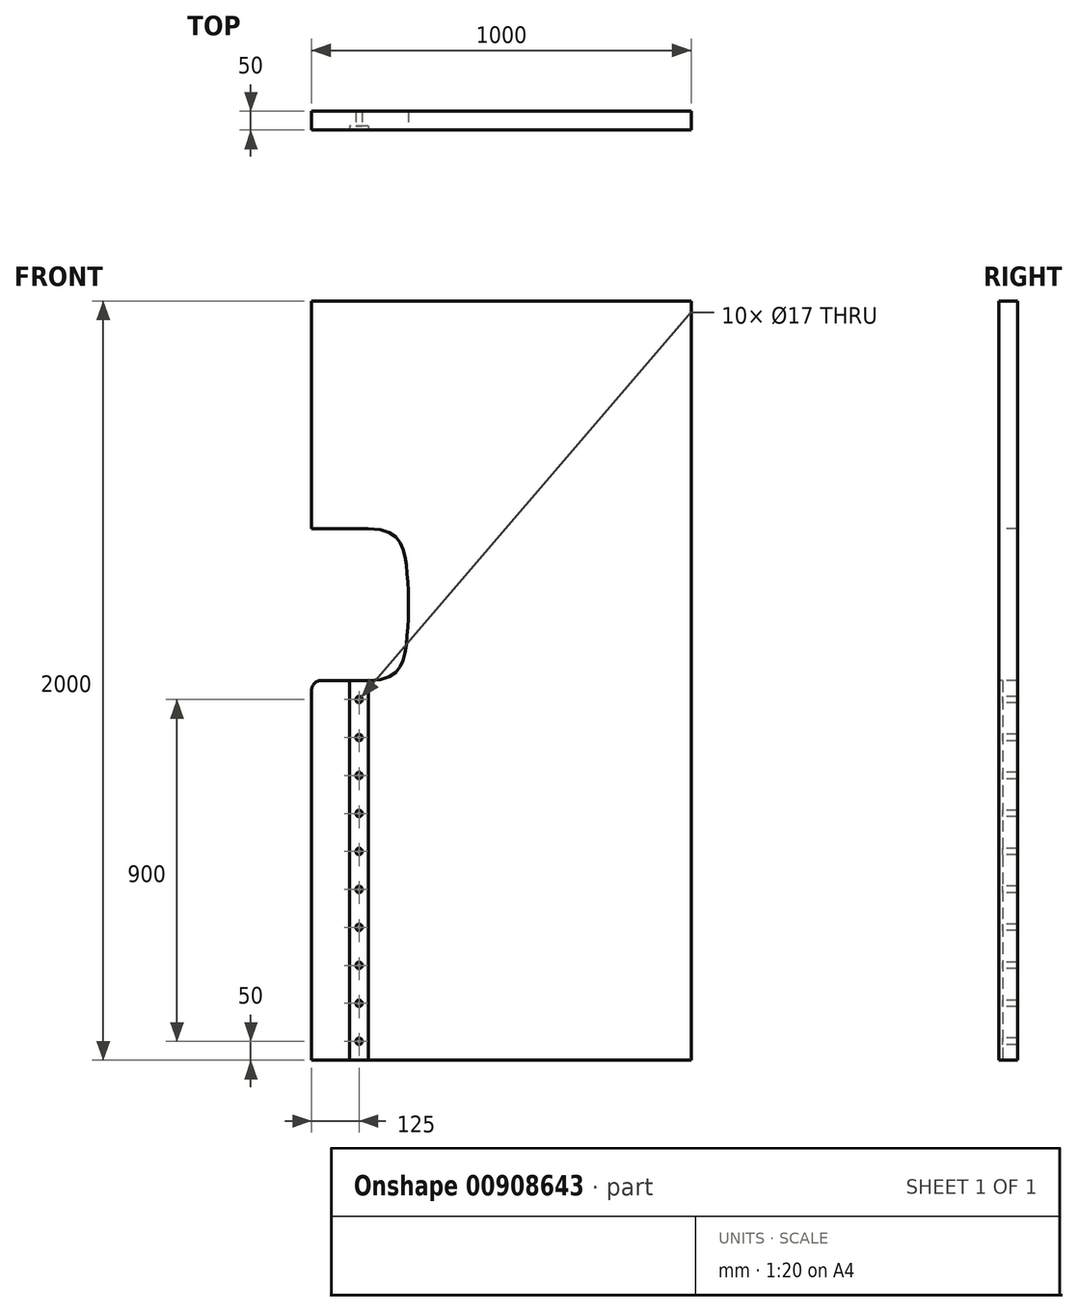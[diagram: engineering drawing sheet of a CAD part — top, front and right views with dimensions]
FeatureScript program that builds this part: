
annotation { "Feature Type Name" : "Feature", "Feature Type Description" : "" }
export const myFeature = defineFeature(function(context is Context, id is Id, definition is map)
    precondition{}
    {
        {
            var Q0;
            Q0=qCreatedBy(makeId("Front.planeOp"),FACE);
            var sketch = newSketch(context, id + "F0", { "sketchPlane" : qUnion([Q0])});
            skLineSegment(sketch, "E0.bottom", {"start": v(500, 1000) * mm, "end": v(-500, 1000) * mm});
            skLineSegment(sketch, "E0.top", {"start": v(500, -1000) * mm, "end": v(-500, -1000) * mm});
            skLineSegment(sketch, "E0.left", {"start": v(500, 1000) * mm, "end": v(500, -1000) * mm});
            skLineSegment(sketch, "E0.right", {"start": v(-500, 1000) * mm, "end": v(-500, -1000) * mm});
            skPoint(sketch, "E0.middle", {"position": v(0, 0) * mm});
            skSolve(sketch);
        }
        {
            var Q0;
            Q0=makeQuery(id+"F0.imprint","IMPRINT",FACE,{"disambiguationData":[TD([[makeQuery(id+"F0.imprint","IMPRINT",EDGE,{"derivedFrom":sQuery(id+"F0.wireOp",EDGE,"E0.bottom")}),1.0]])]});
            extrude(context, id + "F1", {"entities" : qUnion([Q0]), "depth" : 50 * mm, "offsetDistance" : 25 * mm});
        }
        {
            var Q0;
            Q0=makeQuery(id+"F1.opExtrude","CAP_FACE",FACE,{"disambiguationData":[OSD([sQuery(id+"F0.wireOp",EDGE,"E0.bottom"),sQuery(id+"F0.wireOp",EDGE,"E0.top"),sQuery(id+"F0.wireOp",EDGE,"E0.left"),sQuery(id+"F0.wireOp",EDGE,"E0.right")])],"isStart":false});
            var sketch = newSketch(context, id + "F2", { "sketchPlane" : qUnion([Q0])});
            skLineSegment(sketch, "E1.bottom", {"start": v(-400, 0) * mm, "end": v(-350, 0) * mm});
            skLineSegment(sketch, "E1.top", {"start": v(-400, -1000) * mm, "end": v(-350, -1000) * mm});
            skLineSegment(sketch, "E1.left", {"start": v(-400, 0) * mm, "end": v(-400, -1000) * mm});
            skLineSegment(sketch, "E1.right", {"start": v(-350, 0) * mm, "end": v(-350, -1000) * mm});
            skPoint(sketch, "E2.visualSharp", {"position": v(-400, 0) * mm});
            skPoint(sketch, "E3.visualSharp", {"position": v(-350, 0) * mm});
            skSolve(sketch);
        }
        {
            var Q0;
            Q0=makeQuery(id+"F2.imprint","IMPRINT",FACE,{"disambiguationData":[TD([[makeQuery(id+"F2.imprint","IMPRINT",EDGE,{"derivedFrom":sQuery(id+"F2.wireOp",EDGE,"E1.bottom")}),-1.0]])]});
            extrude(context, id + "F3", {"entities" : qUnion([Q0]), "operationType" : NewBodyOperationType.REMOVE, "oppositeDirection" : true, "depth" : 10 * mm, "offsetDistance" : 25 * mm});
        }
        {
            var Q0;
            Q0=makeQuery(id+"F1.opExtrude","CAP_FACE",FACE,{"disambiguationData":[OSD([sQuery(id+"F0.wireOp",EDGE,"E0.bottom"),sQuery(id+"F0.wireOp",EDGE,"E0.top"),sQuery(id+"F0.wireOp",EDGE,"E0.left"),sQuery(id+"F0.wireOp",EDGE,"E0.right")])],"isStart":false});
            var sketch = newSketch(context, id + "F4", { "sketchPlane" : qUnion([Q0])});
            skLineSegment(sketch, "E4", {"start": v(-500, 0) * mm, "end": v(-350, 0) * mm});
            skLineSegment(sketch, "E5", {"start": v(-350, 400) * mm, "end": v(-500, 400) * mm});
            skLineSegment(sketch, "E6", {"start": v(-500, 400) * mm, "end": v(-500, 0) * mm});
            skPoint(sketch, "E7.visualSharp", {"position": v(-250, 0) * mm});
            skPoint(sketch, "E8.visualSharp", {"position": v(-250, 400) * mm});
            skFitSpline(sketch, "E9", {"points": [v(-350, 400) * mm, v(-250, 300) * mm, v(-250, 100) * mm, v(-350, 0) * mm], "startDerivative": vector(804.85, -3.53) * mm, "endDerivative": vector(-804.85, 0) * mm});
            skSolve(sketch);
        }
        {
            var Q0;
            Q0=makeQuery(id+"F4.imprint","IMPRINT",FACE,{"disambiguationData":[TD([[makeQuery(id+"F4.imprint","IMPRINT",EDGE,{"derivedFrom":sQuery(id+"F4.wireOp",EDGE,"E5")}),1.0]])]});
            extrude(context, id + "F5", {"entities" : qUnion([Q0]), "operationType" : NewBodyOperationType.REMOVE, "endBound" : BoundingType.THROUGH_ALL, "oppositeDirection" : true, "depth" : 25 * mm, "offsetDistance" : 25 * mm});
        }
        {
            var Q0;
            Q0=makeQuery(id+"F5.boolean.opBoolean","COPY",EDGE,{"derivedFrom":makeQuery(id+"F5.opExtrude","SWEPT_EDGE",EDGE,{"disambiguationData":[OSD([sQuery(id+"F0.wireOp",EDGE,"E0.right"),sQuery(id+"F4.wireOp",EDGE,"E5"),sQuery(id+"F4.wireOp",EDGE,"E6")])]})});
            var Q1;
            Q1=makeQuery(id+"F5.boolean.opBoolean","COPY",EDGE,{"derivedFrom":makeQuery(id+"F5.opExtrude","SWEPT_EDGE",EDGE,{"disambiguationData":[OSD([sQuery(id+"F0.wireOp",EDGE,"E0.right"),sQuery(id+"F4.wireOp",EDGE,"E4"),sQuery(id+"F4.wireOp",EDGE,"E6")])]})});
            fillet(context, id + "F6", {"entities" : qUnion([Q0, Q1]), "radius" : 25 * mm, "tangentPropagation" : true, "allowEdgeOverflow" : false});
        }
        {
            var Q0;
            Q0=makeQuery(id+"F3.boolean.opBoolean","COPY",FACE,{"derivedFrom":makeQuery(id+"F3.opExtrude","CAP_FACE",FACE,{"disambiguationData":[OSD([sQuery(id+"F2.wireOp",EDGE,"E1.bottom"),sQuery(id+"F2.wireOp",EDGE,"E1.top"),sQuery(id+"F2.wireOp",EDGE,"E1.left"),sQuery(id+"F2.wireOp",EDGE,"E1.right")])],"isStart":false})});
            var sketch = newSketch(context, id + "F7", { "sketchPlane" : qUnion([Q0])});
            skCircle(sketch, "E10", {"center": v(-375, -950) * mm, "radius": 8.5 * mm});
            skCircle(sketch, "E11.0.1.0", {"center": v(-375, -850) * mm, "radius": 8.5 * mm});
            skCircle(sketch, "E11.0.2.0", {"center": v(-375, -750) * mm, "radius": 8.5 * mm});
            skCircle(sketch, "E11.0.3.0", {"center": v(-375, -650) * mm, "radius": 8.5 * mm});
            skCircle(sketch, "E11.0.4.0", {"center": v(-375, -550) * mm, "radius": 8.5 * mm});
            skCircle(sketch, "E11.0.5.0", {"center": v(-375, -450) * mm, "radius": 8.5 * mm});
            skCircle(sketch, "E11.0.6.0", {"center": v(-375, -350) * mm, "radius": 8.5 * mm});
            skCircle(sketch, "E11.0.7.0", {"center": v(-375, -250) * mm, "radius": 8.5 * mm});
            skCircle(sketch, "E11.0.8.0", {"center": v(-375, -150) * mm, "radius": 8.5 * mm});
            skCircle(sketch, "E11.0.9.0", {"center": v(-375, -50) * mm, "radius": 8.5 * mm});
            skLineSegment(sketch, "E11.direction1", {"start": v(-375, -950) * mm, "end": v(-350, -950) * mm, "construction": true});
            skLineSegment(sketch, "E11.direction2", {"start": v(-375, -950) * mm, "end": v(-375, -850) * mm, "construction": true});
            skSolve(sketch);
        }
        {
            var Q0;
            Q0=sQuery(id+"F7.wireOp",VERTEX,"E11.0.9.0.center");
            var Q1;
            Q1=sQuery(id+"F7.wireOp",VERTEX,"E11.0.8.0.center");
            var Q2;
            Q2=sQuery(id+"F7.wireOp",VERTEX,"E11.0.7.0.center");
            var Q3;
            Q3=sQuery(id+"F7.wireOp",VERTEX,"E11.0.6.0.center");
            var Q4;
            Q4=sQuery(id+"F7.wireOp",VERTEX,"E11.0.5.0.center");
            var Q5;
            Q5=sQuery(id+"F7.wireOp",VERTEX,"E11.0.4.0.center");
            var Q6;
            Q6=sQuery(id+"F7.wireOp",VERTEX,"E11.0.3.0.center");
            var Q7;
            Q7=sQuery(id+"F7.wireOp",VERTEX,"E11.0.2.0.center");
            var Q8;
            Q8=sQuery(id+"F7.wireOp",VERTEX,"E11.direction2.end");
            var Q9;
            Q9=sQuery(id+"F7.wireOp",VERTEX,"E11.direction1.start");
            var Q10;
            Q10=makeQuery(id+"F1.opExtrude","SWEPT_BODY",BODY,{"disambiguationData":[OSD([sQuery(id+"F0.wireOp",EDGE,"E0.bottom"),sQuery(id+"F0.wireOp",EDGE,"E0.top"),sQuery(id+"F0.wireOp",EDGE,"E0.left"),sQuery(id+"F0.wireOp",EDGE,"E0.right")])]});
            hole(context, id + "F8", {"style" : HoleStyle.SIMPLE, "endStyle" : HoleEndStyle.THROUGH, "holeDiameter" : 17 * mm, "majorDiameter" : 16 * mm, "isTappedThrough" : true, "tappedDepth" : 25 * mm, "tapClearance" : 3, "startFromSketch" : true, "locations" : qUnion([Q0, Q1, Q2, Q3, Q4, Q5, Q6, Q7, Q8, Q9]), "scope" : qUnion([Q10])});
        }
    });
